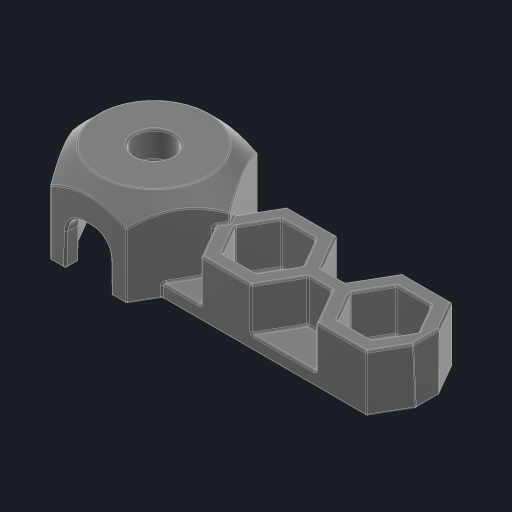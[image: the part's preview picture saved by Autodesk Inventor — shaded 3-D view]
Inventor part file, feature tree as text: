
AUTODESK INVENTOR PART (.ipt)
format: ipt  version: 2023 (Build 270158030, 158C)  size: 676,352 bytes
history: native  units: in
note: dims shown in document units (in); Inventor stores cm internally (conversion verified against a paired STEP export)
features: extrude x1, sketch x1, fillet x1
ambient origin geometry x8: Origin, YZ Plane, XZ Plane, XY Plane, X Axis, Y Axis, Z Axis, Center Point
bodies: Solid1 (feature_tree)
feature tree (3):
  extrude  "Extrusion1"  [1 undecoded]
  sketch  "Sketch1"  dims[d0=0.0394in d1=0.0in]
  fillet  "Fillet23"  [1 undecoded]
note: 2 required parameter values undecoded (feature->parameter linkage not recoverable at this tier; creation-order binding heuristic only, values carry confidence <= 0.55)
